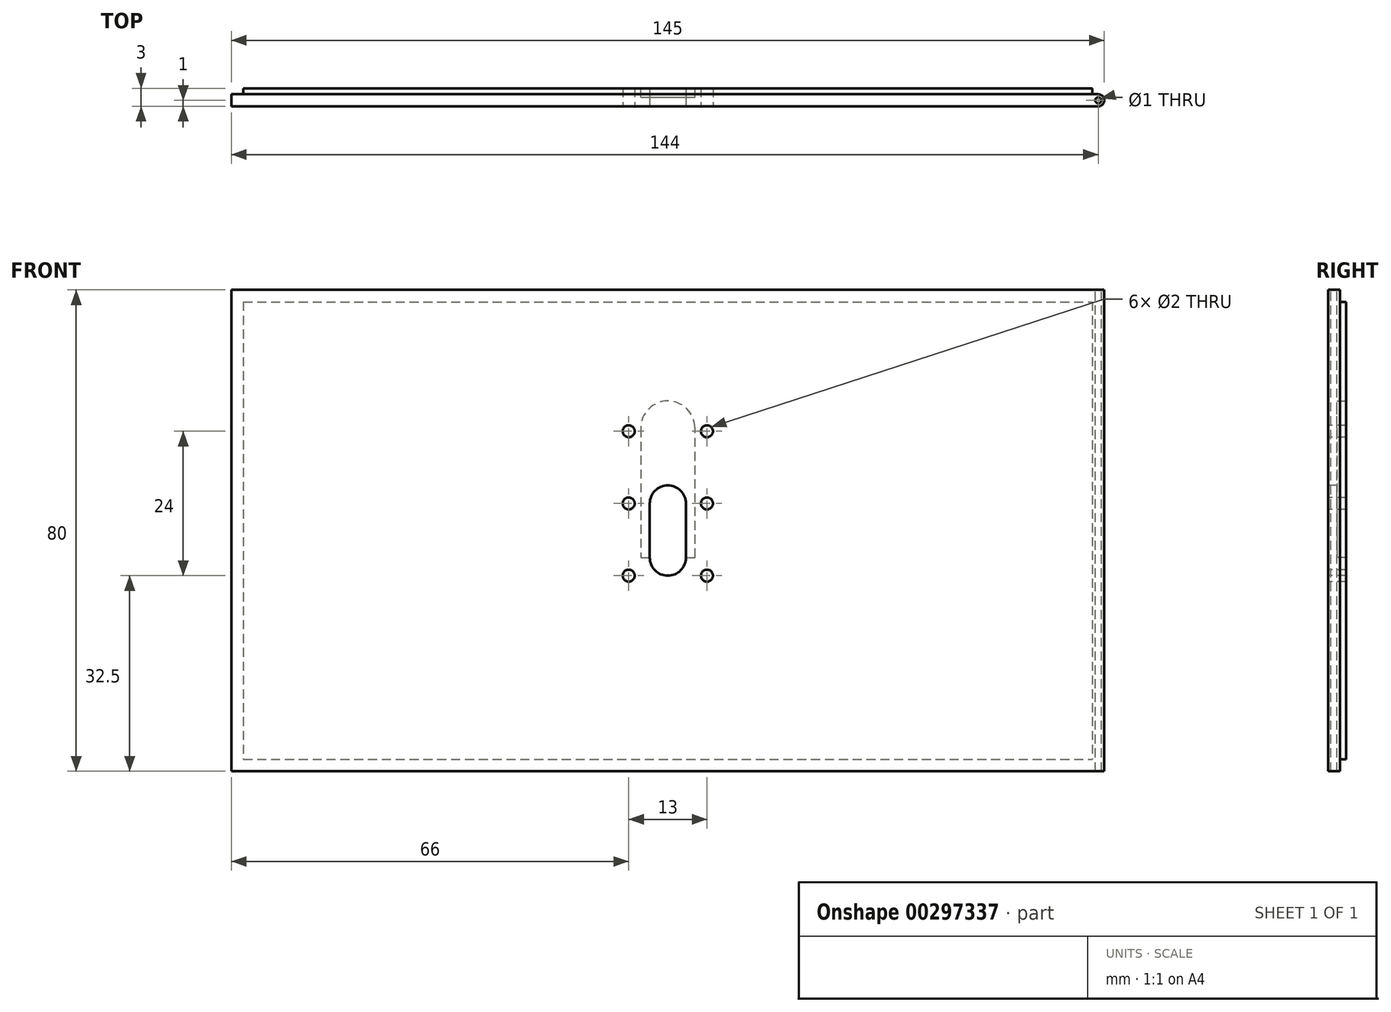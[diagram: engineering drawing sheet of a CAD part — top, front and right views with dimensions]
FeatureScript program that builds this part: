
annotation { "Feature Type Name" : "Feature", "Feature Type Description" : "" }
export const myFeature = defineFeature(function(context is Context, id is Id, definition is map)
    precondition{}
    {
        {
            var Q0;
            Q0=qCreatedBy(makeId("Front.planeOp"),FACE);
            var sketch = newSketch(context, id + "F0", { "sketchPlane" : qUnion([Q0])});
            skLineSegment(sketch, "E0.bottom", {"start": v(72.5, 40) * mm, "end": v(-72.5, 40) * mm});
            skLineSegment(sketch, "E0.top", {"start": v(72.5, -40) * mm, "end": v(-72.5, -40) * mm});
            skLineSegment(sketch, "E0.left", {"start": v(72.5, 40) * mm, "end": v(72.5, -40) * mm});
            skLineSegment(sketch, "E0.right", {"start": v(-72.5, 40) * mm, "end": v(-72.5, -40) * mm});
            skPoint(sketch, "E0.middle", {"position": v(0, 0) * mm});
            skSolve(sketch);
        }
        {
            var Q0;
            Q0=qSketchRegion(id+"F0",true);
            extrude(context, id + "F1", {"entities" : qUnion([Q0]), "depth" : 2 * mm});
        }
        {
            var Q0;
            Q0=makeQuery(id+"F1.opExtrude","CAP_FACE",FACE,{"disambiguationData":[OSD([sQuery(id+"F0.wireOp",EDGE,"E0.bottom"),sQuery(id+"F0.wireOp",EDGE,"E0.top"),sQuery(id+"F0.wireOp",EDGE,"E0.left"),sQuery(id+"F0.wireOp",EDGE,"E0.right")])],"isStart":true});
            var sketch = newSketch(context, id + "F2", { "sketchPlane" : qUnion([Q0])});
            skLineSegment(sketch, "E1.bottom", {"start": v(70.5, 38) * mm, "end": v(-70.5, 38) * mm});
            skLineSegment(sketch, "E1.top", {"start": v(70.5, -38) * mm, "end": v(-70.5, -38) * mm});
            skLineSegment(sketch, "E1.left", {"start": v(70.5, 38) * mm, "end": v(70.5, -38) * mm});
            skLineSegment(sketch, "E1.right", {"start": v(-70.5, 38) * mm, "end": v(-70.5, -38) * mm});
            skPoint(sketch, "E1.middle", {"position": v(0, 0) * mm});
            skSolve(sketch);
        }
        {
            var Q0;
            Q0=qSketchRegion(id+"F2",true);
            extrude(context, id + "F3", {"entities" : qUnion([Q0]), "operationType" : NewBodyOperationType.ADD, "depth" : 1 * mm});
        }
        {
            var Q0;
            Q0=makeQuery(id+"F1.opExtrude","CAP_FACE",FACE,{"disambiguationData":[OSD([sQuery(id+"F0.wireOp",EDGE,"E0.bottom"),sQuery(id+"F0.wireOp",EDGE,"E0.top"),sQuery(id+"F0.wireOp",EDGE,"E0.left"),sQuery(id+"F0.wireOp",EDGE,"E0.right")])],"isStart":false});
            var sketch = newSketch(context, id + "F4", { "sketchPlane" : qUnion([Q0])});
            skLineSegment(sketch, "E2.left", {"start": v(3, 4.5) * mm, "end": v(3, -4.5) * mm});
            skLineSegment(sketch, "E2.right", {"start": v(-3, 4.5) * mm, "end": v(-3, -4.5) * mm});
            skPoint(sketch, "E2.middle", {"position": v(0, 0) * mm});
            skArc(sketch, "E3", {"start": v(3, 4.5) * mm, "mid": v(0, 7.5) * mm, "end": v(-3, 4.5) * mm});
            skArc(sketch, "E4", {"start": v(-3, -4.5) * mm, "mid": v(0, -7.5) * mm, "end": v(3, -4.5) * mm});
            skSolve(sketch);
        }
        {
            var Q0;
            Q0=qSketchRegion(id+"F4",true);
            extrude(context, id + "F5", {"entities" : qUnion([Q0]), "operationType" : NewBodyOperationType.REMOVE, "oppositeDirection" : true, "depth" : 25 * mm});
        }
        {
            var Q0;
            Q0=makeQuery(id+"F1.opExtrude","CAP_FACE",FACE,{"disambiguationData":[OSD([sQuery(id+"F0.wireOp",EDGE,"E0.bottom"),sQuery(id+"F0.wireOp",EDGE,"E0.top"),sQuery(id+"F0.wireOp",EDGE,"E0.left"),sQuery(id+"F0.wireOp",EDGE,"E0.right")])],"isStart":false});
            var sketch = newSketch(context, id + "F6", { "sketchPlane" : qUnion([Q0])});
            skLineSegment(sketch, "E5.bottom", {"start": v(-6.5, 16.5) * mm, "end": v(6.5, 16.5) * mm, "construction": true});
            skLineSegment(sketch, "E5.top", {"start": v(-6.5, -7.5) * mm, "end": v(6.5, -7.5) * mm, "construction": true});
            skLineSegment(sketch, "E5.left", {"start": v(-6.5, 16.5) * mm, "end": v(-6.5, -7.5) * mm, "construction": true});
            skLineSegment(sketch, "E5.right", {"start": v(6.5, 16.5) * mm, "end": v(6.5, -7.5) * mm, "construction": true});
            skCircle(sketch, "E6", {"center": v(-6.5, 16.5) * mm, "radius": 1 * mm});
            skCircle(sketch, "E7", {"center": v(6.5, 16.5) * mm, "radius": 1 * mm});
            skCircle(sketch, "E8", {"center": v(6.5, -7.5) * mm, "radius": 1 * mm});
            skCircle(sketch, "E9", {"center": v(-6.5, -7.5) * mm, "radius": 1 * mm});
            skCircle(sketch, "E10", {"center": v(-6.5, 4.5) * mm, "radius": 1 * mm});
            skCircle(sketch, "E11", {"center": v(6.5, 4.5) * mm, "radius": 1 * mm});
            skSolve(sketch);
        }
        {
            var Q0;
            Q0=qSketchRegion(id+"F6",true);
            extrude(context, id + "F7", {"entities" : qUnion([Q0]), "operationType" : NewBodyOperationType.REMOVE, "oppositeDirection" : true, "depth" : 25 * mm});
        }
        {
            var Q0;
            Q0=makeQuery(id+"F1.opExtrude","SWEPT_FACE",FACE,{"disambiguationData":[OSD([sQuery(id+"F0.wireOp",EDGE,"E0.bottom")])]});
            var sketch = newSketch(context, id + "F8", { "sketchPlane" : qUnion([Q0])});
            skLineSegment(sketch, "E12.bottom", {"start": v(72.5, 0) * mm, "end": v(71.5, 0) * mm});
            skLineSegment(sketch, "E12.top", {"start": v(72.5, -2) * mm, "end": v(71.5, -2) * mm});
            skLineSegment(sketch, "E12.left", {"start": v(72.5, 0) * mm, "end": v(72.5, -2) * mm});
            skLineSegment(sketch, "E12.right", {"start": v(71.5, 0) * mm, "end": v(71.5, -2) * mm});
            skSolve(sketch);
        }
        {
            var Q0;
            Q0 = qSketchRegion(id + "F8", true);
            extrude(context, id + "F9", {"entities" : qUnion([Q0]), "operationType" : NewBodyOperationType.REMOVE, "oppositeDirection" : true, "depth" : 200 * mm});
        }
        {
            var Q0;
            Q0=makeQuery(id+"F1.opExtrude","SWEPT_FACE",FACE,{"disambiguationData":[OSD([sQuery(id+"F0.wireOp",EDGE,"E0.bottom")])]});
            var sketch = newSketch(context, id + "F10", { "sketchPlane" : qUnion([Q0])});
            skCircle(sketch, "E13", {"center": v(71.5, -1) * mm, "radius": 1 * mm});
            skSolve(sketch);
        }
        {
            var Q0;
            Q0 = qSketchRegion(id + "F10", true);
            extrude(context, id + "F11", {"entities" : qUnion([Q0]), "operationType" : NewBodyOperationType.ADD, "oppositeDirection" : true, "depth" : 80 * mm});
        }
        {
            var Q0;
            Q0=makeQuery(id+"F11.boolean.opBoolean","MERGE",FACE,{"derivedFrom":[makeQuery(id+"F1.opExtrude","SWEPT_FACE",FACE,{"disambiguationData":[OSD([sQuery(id+"F0.wireOp",EDGE,"E0.bottom")])]}),makeQuery(id+"F11.opExtrude","CAP_FACE",FACE,{"disambiguationData":[OSD([sQuery(id+"F10.wireOp",EDGE,"E13")])],"isStart":true})]});
            var sketch = newSketch(context, id + "F12", { "sketchPlane" : qUnion([Q0])});
            skCircle(sketch, "E14", {"center": v(71.5, -1) * mm, "radius": 0.5 * mm});
            skSolve(sketch);
        }
        {
            var Q0;
            Q0 = qSketchRegion(id + "F12", true);
            extrude(context, id + "F13", {"entities" : qUnion([Q0]), "operationType" : NewBodyOperationType.REMOVE, "oppositeDirection" : true, "depth" : 300 * mm});
        }
        {
            var Q0;
            Q0=makeQuery(id+"F3.opExtrude","CAP_FACE",FACE,{"disambiguationData":[OSD([sQuery(id+"F2.wireOp",EDGE,"E1.bottom"),sQuery(id+"F2.wireOp",EDGE,"E1.top"),sQuery(id+"F2.wireOp",EDGE,"E1.left"),sQuery(id+"F2.wireOp",EDGE,"E1.right")])],"isStart":false});
            var sketch = newSketch(context, id + "F14", { "sketchPlane" : qUnion([Q0])});
            skPoint(sketch, "E15.middle", {"position": v(0, 0) * mm});
            skLineSegment(sketch, "E16.bottom", {"start": v(-3, -4.5) * mm, "end": v(-4.5, -4.5) * mm});
            skLineSegment(sketch, "E16.right", {"start": v(-4.5, -4.5) * mm, "end": v(-4.5, 17.04) * mm});
            skLineSegment(sketch, "E17.top", {"start": v(3, -4.5) * mm, "end": v(4.5, -4.5) * mm});
            skLineSegment(sketch, "E17.right", {"start": v(4.5, 17.04) * mm, "end": v(4.5, -4.5) * mm});
            skArc(sketch, "E18", {"start": v(4.5, 17.04) * mm, "mid": v(0, 21.54) * mm, "end": v(-4.5, 17.04) * mm});
            skLineSegment(sketch, "E19", {"start": v(-3, -4.5) * mm, "end": v(3, -4.5) * mm});
            skSolve(sketch);
        }
        {
            var Q0;
            Q0 = qSketchRegion(id + "F14", true);
            extrude(context, id + "F15", {"entities" : qUnion([Q0]), "operationType" : NewBodyOperationType.REMOVE, "oppositeDirection" : true, "depth" : 1.5 * mm});
        }
    });
